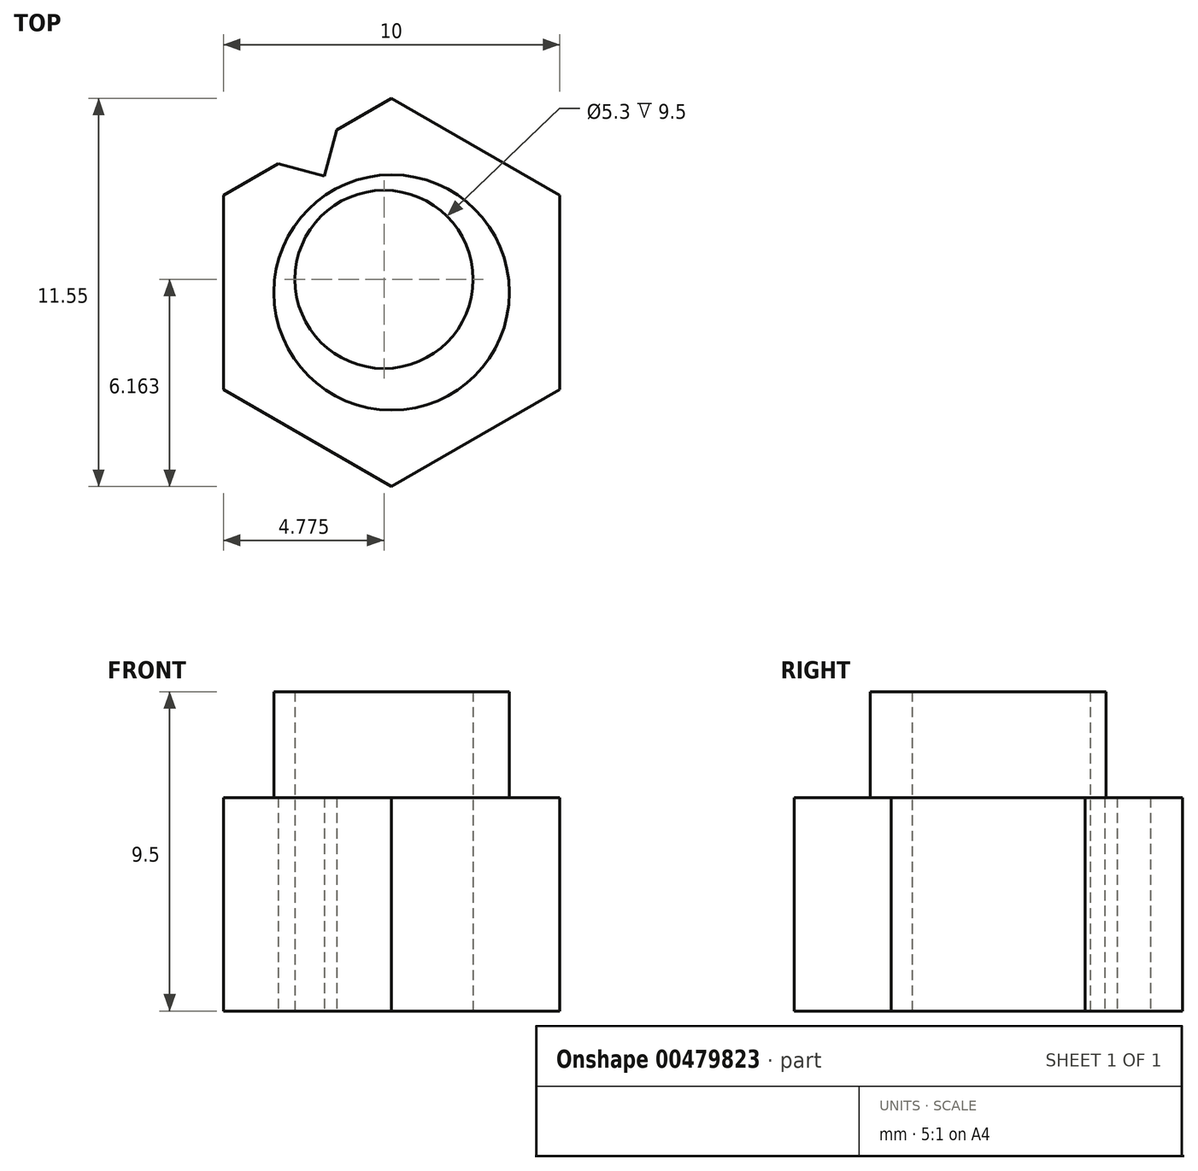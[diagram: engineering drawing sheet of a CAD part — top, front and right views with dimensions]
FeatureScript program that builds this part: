
annotation { "Feature Type Name" : "Feature", "Feature Type Description" : "" }
export const myFeature = defineFeature(function(context is Context, id is Id, definition is map)
    precondition{}
    {
        {
            var Q0;
            Q0=qCreatedBy(makeId("Top.planeOp"),FACE);
            var sketch = newSketch(context, id + "F0", { "sketchPlane" : qUnion([Q0])});
            skLineSegment(sketch, "E0", {"start": v(0, 0) * mm, "end": v(0, -5.77) * mm});
            skLineSegment(sketch, "E1", {"start": v(0, -5.77) * mm, "end": v(5, -8.66) * mm});
            skLineSegment(sketch, "E2", {"start": v(5, -8.66) * mm, "end": v(10, -5.77) * mm});
            skLineSegment(sketch, "E3", {"start": v(10, -5.77) * mm, "end": v(10, 0) * mm});
            skLineSegment(sketch, "E4", {"start": v(10, 0) * mm, "end": v(5, 2.89) * mm});
            skLineSegment(sketch, "E5", {"start": v(5, 2.89) * mm, "end": v(0, 0) * mm});
            skLineSegment(sketch, "E6", {"start": v(0, 0) * mm, "end": v(10, -5.77) * mm, "construction": true});
            skPoint(sketch, "E7", {"position": v(5, -2.89) * mm});
            skCircle(sketch, "E8", {"center": v(5, -2.89) * mm, "radius": 3.5 * mm});
            skCircle(sketch, "E9", {"center": v(4.78, -2.5) * mm, "radius": 2.65 * mm});
            skLineSegment(sketch, "E10", {"start": v(2.5, 1.44) * mm, "end": v(7.5, -7.22) * mm, "construction": true});
            skPoint(sketch, "E11", {"position": v(3, 0.58) * mm});
            skLineSegment(sketch, "E12", {"start": v(3, 0.58) * mm, "end": v(3.37, 1.94) * mm});
            skLineSegment(sketch, "E13", {"start": v(3, 0.58) * mm, "end": v(1.63, 0.94) * mm});
            skSolve(sketch);
        }
        {
            var Q0;
            Q0=makeQuery(id+"F0.imprint","IMPRINT",FACE,{"disambiguationData":[TD([[makeQuery(id+"F0.imprint","IMPRINT",EDGE,{"derivedFrom":sQuery(id+"F0.wireOp",EDGE,"E9")}),1.0]])]});
            var Q1;
            Q1=makeQuery(id+"F0.imprint","IMPRINT",FACE,{"disambiguationData":[TD([[makeQuery(id+"F0.imprint","IMPRINT",EDGE,{"derivedFrom":sQuery(id+"F0.wireOp",EDGE,"E8")}),1.0]])]});
            extrude(context, id + "F1", {"entities" : qUnion([Q0, Q1]), "depth" : 9.5 * mm});
        }
        {
            var Q0;
            Q0=makeQuery(id+"F0.imprint","IMPRINT",FACE,{"disambiguationData":[TD([[makeQuery(id+"F0.imprint","IMPRINT",EDGE,{"derivedFrom":sQuery(id+"F0.wireOp",EDGE,"E0")}),1.0]])]});
            extrude(context, id + "F2", {"entities" : qUnion([Q0]), "operationType" : NewBodyOperationType.ADD, "depth" : 6.35 * mm});
        }
        {
            var Q0;
            Q0=makeQuery(id+"F0.imprint","IMPRINT",FACE,{"disambiguationData":[TD([[makeQuery(id+"F0.imprint","IMPRINT",EDGE,{"derivedFrom":sQuery(id+"F0.wireOp",EDGE,"E9")}),1.0]])]});
            extrude(context, id + "F3", {"entities" : qUnion([Q0]), "operationType" : NewBodyOperationType.REMOVE, "endBound" : BoundingType.THROUGH_ALL, "depth" : 25 * mm});
        }
    });
